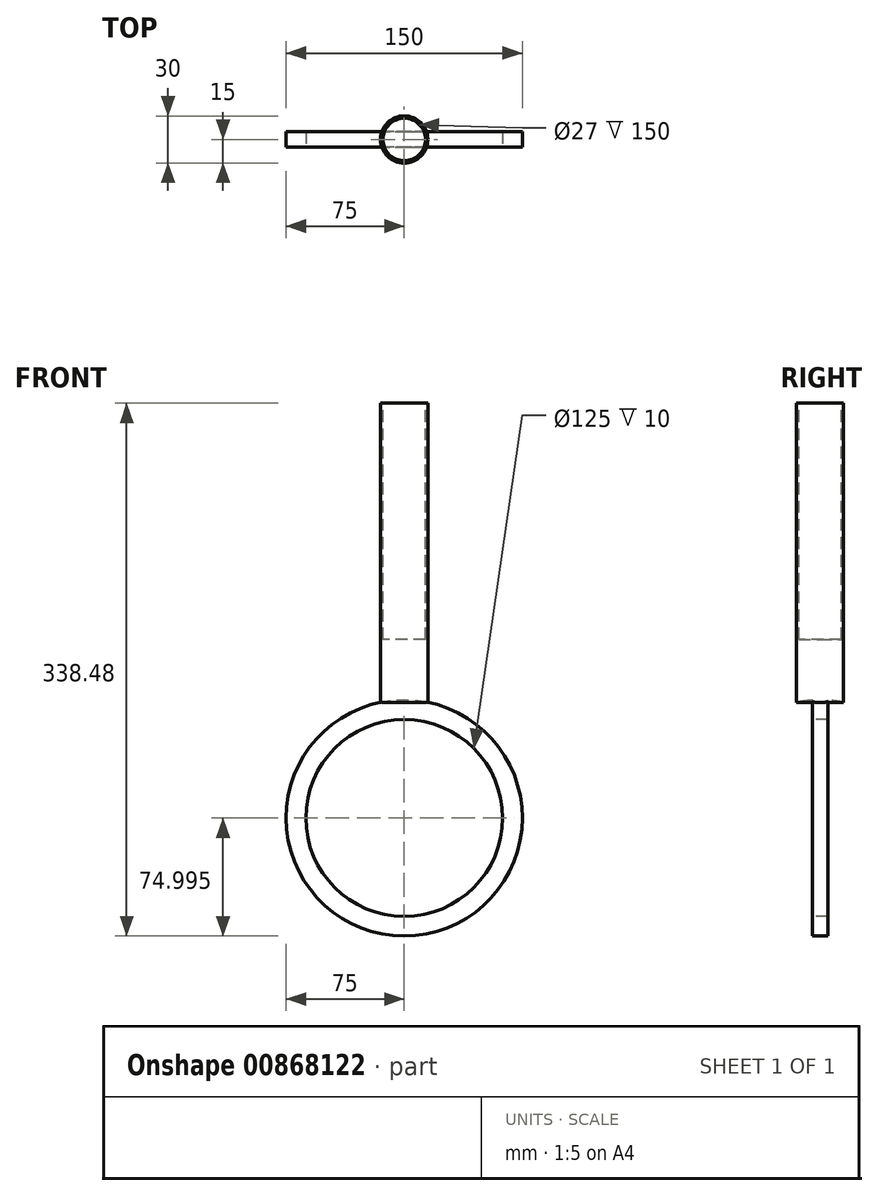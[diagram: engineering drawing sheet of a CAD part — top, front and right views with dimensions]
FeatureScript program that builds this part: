
annotation { "Feature Type Name" : "Feature", "Feature Type Description" : "" }
export const myFeature = defineFeature(function(context is Context, id is Id, definition is map)
    precondition{}
    {
        {
            var Q0;
            Q0=qCreatedBy(makeId("Front.planeOp"),FACE);
            var sketch = newSketch(context, id + "F0", { "sketchPlane" : qUnion([Q0])});
            skLineSegment(sketch, "E0", {"start": v(0, 0) * mm, "end": v(0, 190) * mm});
            skLineSegment(sketch, "E1", {"start": v(0, 190) * mm, "end": v(-15, 190) * mm});
            skLineSegment(sketch, "E2", {"start": v(-15, 190) * mm, "end": v(-15, 0) * mm});
            skLineSegment(sketch, "E3", {"start": v(-15, 0) * mm, "end": v(0, 0) * mm});
            skCircle(sketch, "E4", {"center": v(0, -73.48) * mm, "radius": 75 * mm});
            skLineSegment(sketch, "E5", {"start": v(0, 196.25) * mm, "end": v(0, -33.97) * mm, "construction": true});
            skSolve(sketch);
        }
        {
            var Q0;
            {var subQ0=sQuery(id+"F0.wireOp",EDGE,"E1");Q0=makeQuery(id+"F0.imprint","IMPRINT",FACE,{"disambiguationData":[TD([[makeQuery(id+"F0.imprint","IMPRINT",EDGE,{"derivedFrom":subQ0}),1.0]])]});}
            var Q1;
            Q1=sQuery(id+"F0.wireOp",EDGE,"E5");
            revolve(context, id + "F1", {"surfaceOperationType" : NewSurfaceOperationType.NEW, "entities" : qUnion([Q0]), "axis" : qUnion([Q1]), "revolveType" : RevolveType.FULL});
        }
        {
            var Q0;
            {var subQ0=sQuery(id+"F0.wireOp",EDGE,"E3");Q0=makeQuery(id+"F0.imprint","IMPRINT",FACE,{"disambiguationData":[TD([[makeQuery(id+"F0.imprint","IMPRINT",EDGE,{"derivedFrom":subQ0}),1.0]])]});}
            var Q1;
            {var subQ0=sQuery(id+"F0.wireOp",EDGE,"E3");Q1=makeQuery(id+"F0.imprint","IMPRINT",FACE,{"disambiguationData":[TD([[makeQuery(id+"F0.imprint","IMPRINT",EDGE,{"derivedFrom":subQ0}),-1.0]])]});}
            extrude(context, id + "F2", {"entities" : qUnion([Q0, Q1]), "operationType" : NewBodyOperationType.ADD, "endBound" : BoundingType.SYMMETRIC, "depth" : 10 * mm, "offsetDistance" : 25 * mm});
        }
        {
            var Q0;
            Q0=makeQuery(id+"F2.opExtrude","CAP_FACE",FACE,{"disambiguationData":[OSD([sQuery(id+"F0.wireOp",EDGE,"E4")])],"isStart":false});
            var sketch = newSketch(context, id + "F3", { "sketchPlane" : qUnion([Q0])});
            skCircle(sketch, "E6", {"center": v(0, -73.48) * mm, "radius": 62.5 * mm});
            skSolve(sketch);
        }
        {
            var Q0;
            Q0=makeQuery(id+"F3.imprint","IMPRINT",FACE,{"disambiguationData":[TD([[makeQuery(id+"F3.imprint","IMPRINT",EDGE,{"derivedFrom":sQuery(id+"F3.wireOp",EDGE,"E6")}),1.0]])]});
            extrude(context, id + "F4", {"entities" : qUnion([Q0]), "operationType" : NewBodyOperationType.REMOVE, "oppositeDirection" : true, "depth" : 25 * mm, "offsetDistance" : 25 * mm});
        }
        {
            var Q0;
            Q0=makeQuery(id+"F1.opRevolve","SWEPT_FACE",FACE,{"disambiguationData":[OSD([sQuery(id+"F0.wireOp",EDGE,"E1")])]});
            var sketch = newSketch(context, id + "F5", { "sketchPlane" : qUnion([Q0])});
            skCircle(sketch, "E7", {"center": v(0, 0) * mm, "radius": 13.5 * mm});
            skSolve(sketch);
        }
        {
            var Q0;
            Q0=makeQuery(id+"F5.imprint","IMPRINT",FACE,{"disambiguationData":[TD([[makeQuery(id+"F5.imprint","IMPRINT",EDGE,{"derivedFrom":sQuery(id+"F5.wireOp",EDGE,"E7")}),1.0]])]});
            extrude(context, id + "F6", {"entities" : qUnion([Q0]), "operationType" : NewBodyOperationType.REMOVE, "oppositeDirection" : true, "depth" : 150 * mm, "offsetDistance" : 25 * mm});
        }
    });
